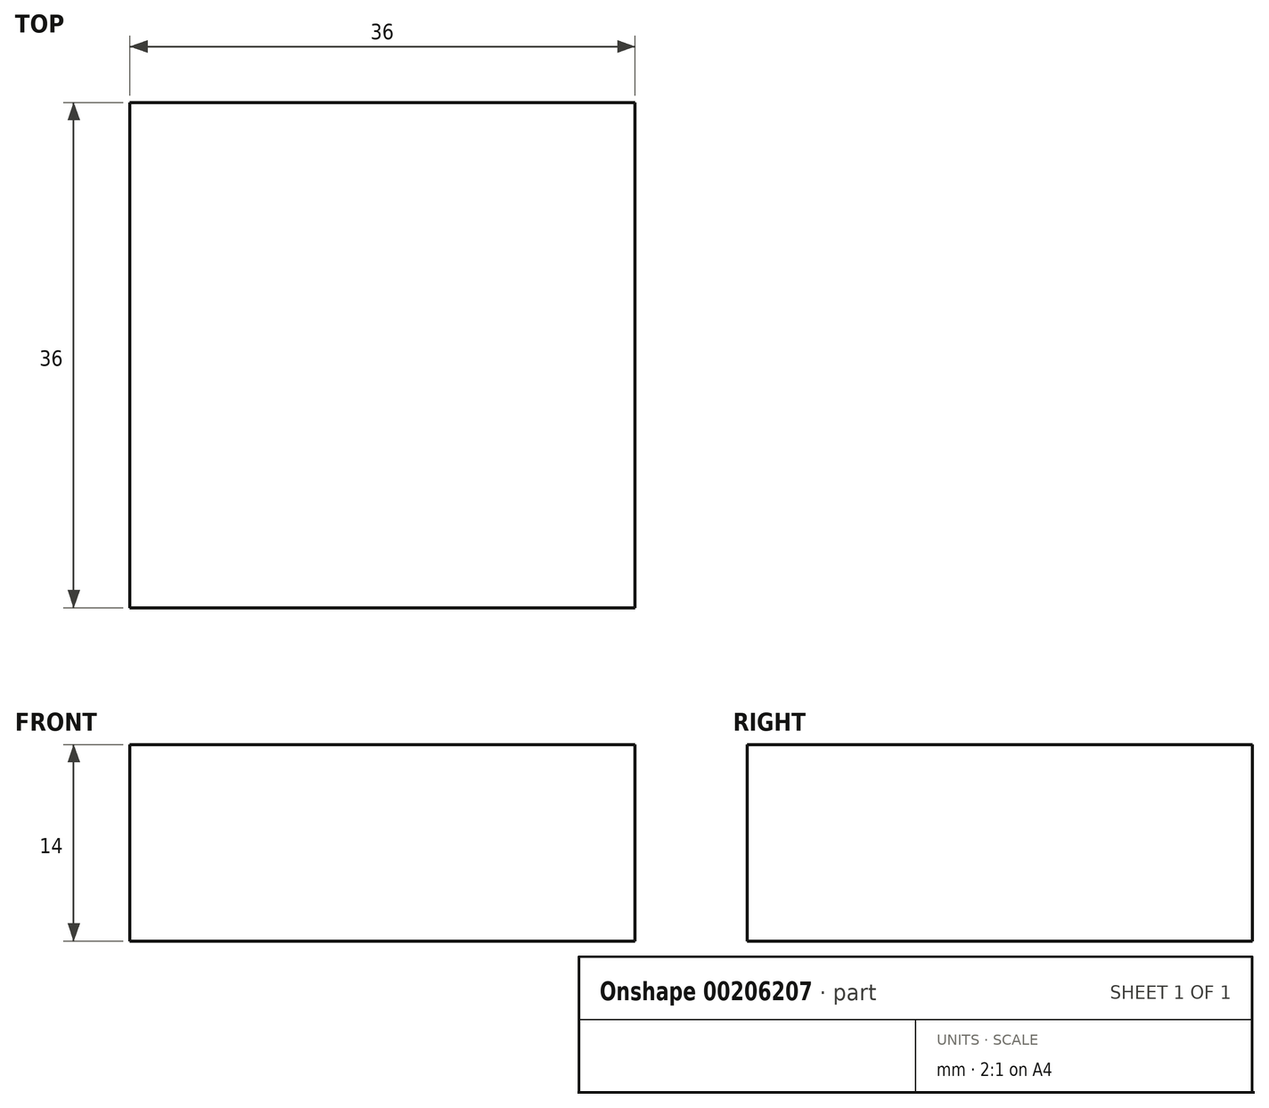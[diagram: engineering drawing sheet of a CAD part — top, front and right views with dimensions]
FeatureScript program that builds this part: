
annotation { "Feature Type Name" : "Feature", "Feature Type Description" : "" }
export const myFeature = defineFeature(function(context is Context, id is Id, definition is map)
    precondition{}
    {
        {
            var Q0;
            Q0=qCreatedBy(makeId("Top.planeOp"),FACE);
            var sketch = newSketch(context, id + "F0", { "sketchPlane" : qUnion([Q0])});
            skLineSegment(sketch, "E0.bottom", {"start": v(18, 18) * mm, "end": v(-18, 18) * mm});
            skLineSegment(sketch, "E0.top", {"start": v(18, -18) * mm, "end": v(-18, -18) * mm});
            skLineSegment(sketch, "E0.left", {"start": v(18, 18) * mm, "end": v(18, -18) * mm});
            skLineSegment(sketch, "E0.right", {"start": v(-18, 18) * mm, "end": v(-18, -18) * mm});
            skPoint(sketch, "E0.middle", {"position": v(0, 0) * mm});
            skSolve(sketch);
        }
        {
            var Q0;
            Q0=makeQuery(id+"F0.imprint","IMPRINT",FACE,{"disambiguationData":[TD([[makeQuery(id+"F0.imprint","IMPRINT",EDGE,{"derivedFrom":sQuery(id+"F0.wireOp",EDGE,"E0.bottom")}),1.0]])]});
            extrude(context, id + "F1", {"entities" : qUnion([Q0]), "depth" : 14 * mm});
        }
    });
